# Revit family: Wall Acoustic Batt (R2.2)
name_source: partatom
category: Structural Stiffeners
units: mm (PartAtom-declared; Revit-internal decimal feet)

## family parameters
Cut with Voids When Loaded = No
OmniClass Number = 23.25.30.11.27
OmniClass Title = Vibration and Earthquake Controls
Shared = No

## types (2) — shared parameters
Description = Ecowool Wall Acoustic Batts is semi-rigid or rigid slabs of non-combustible, water repellent, glass mineral wool. They are designed to suit internal walls and ceiling of residential, commercial and industrial buildings. Excellent thermal, acoustic and fire safety performance
Finish = Wall Acoustic Batt
Gypsum Thickness (mm) = 13 mm
Height Wall (mm) = 2500 mm  [stored 8.2021 ft]
Insulation Length (mm) = 609 mm  [stored 1.99803 ft]
Insulation Thickness (mm) = 75 mm  [stored 0.246063 ft]
Manufacturer = PGF Insulation Sdn. Bhd.
Metal Stud Spacer (mm) = 609 mm  [stored 1.99803 ft]
Metal Stud Width = 75 mm  [stored 0.246063 ft]
Model = Wall Acoustic Batt
Thermal R Value = 2.2
Type of Insulation = Glass Mineral Wool Blanket with vapour barrier
URL = www.ecowool.com.au
zero-valued in all types: Typical weight of ECOWOOL-Kg/M2, U-Value W/m2k

## per-type parameters (varying)
| type | Density | ECOWOOL Product thickness in mm | Thermal K Value | Total System Thickness-mm |
| 75mm | 13.00 kg/m³ | 75 x 13.000000 kg/m³ | 0.0396 | 75 mm  [stored 0.246063 ft] |
| R2.2 - Wall Acoustic Batts | 32.00 kg/m³ | 75 x 32.000000 kg/m³ | 0.0327 | 90 mm  [stored 0.295276 ft] |

note: [stored X ft] marks values corroborated as IEEE doubles in the binary element streams (Revit-internal decimal feet)

## geometry (parser evidence)
native form markers: Sweep x15
no freeform markers — native parametric forms only
